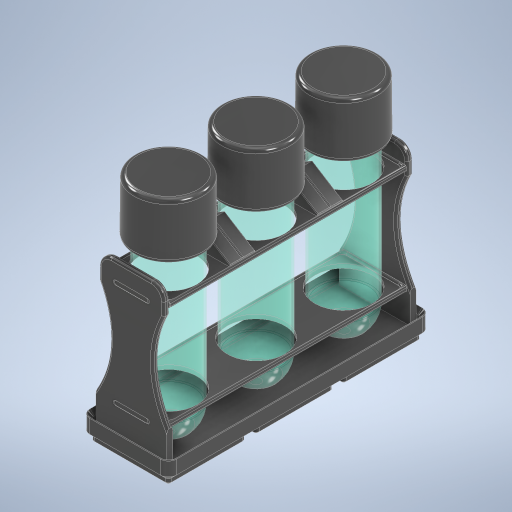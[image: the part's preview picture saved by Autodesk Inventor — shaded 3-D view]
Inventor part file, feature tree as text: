
AUTODESK INVENTOR PART (.ipt)
format: ipt  version: 2023 (Build 270158030, 158C)  size: 1,601,024 bytes
history: native  units: mm
features: extrude x23, sketch x21, other x17, fillet x17, projected_geometry x8, plane x6, chamfer x4, pattern_linear x3, mirror x2
ambient origin geometry x8: Origin, YZ Plane, XZ Plane, XY Plane, X Axis, Y Axis, Z Axis, Center Point
bodies: Body1 (feature_tree), Body2 (feature_tree), Body3 (feature_tree), Body4 (feature_tree), Body5 (feature_tree), Body6 (feature_tree), Body7 (feature_tree), Body8 (feature_tree), Body9 (feature_tree), Body10 (feature_tree), Body11 (feature_tree)
feature tree (101):
  other  "rack"
  extrude  "base-generic"  Depth=41.5mm
  extrude  "Extrusion8"  Depth=2.25mm TaperAngle=0.0deg
  extrude  "Extrusion9"  Depth=2.15mm
  extrude  "Extrusion10"  Depth=0.8mm
  extrude  "Extrusion11"  Depth=7.75mm
  extrude  "Extrusion12"  Depth=7.75mm
  plane  "Work Plane3"
  extrude  "Extrusion15"  Depth=2.4mm TaperAngle=0.0deg
  fillet  "Fillet3"  Radius=3.0mm
  extrude  "Extrusion16"  Depth=10.0mm
  fillet  "Fillet4"  Radius=2.25mm
  extrude  "Extrusion17"  Depth=35.592094mm
  fillet  "Fillet5"  Radius=15.0mm
  pattern_linear  "Rectangular Pattern1"  Spacing1=20.75mm  [1 undecoded]
  plane  "Work Plane8"
  sketch  "Sketch17"  dims[d66=7.75mm d67=2.4mm d68=0.0mm d69=3.0mm]
  extrude  "Extrusion18"  Depth=0.3mm
  pattern_linear  "Rectangular Pattern2"  Spacing1=26.75mm  [1 undecoded]
  plane  "Work Plane4"
  extrude  "Extrusion19"  Depth=2.0mm
  plane  "Work Plane6"
  extrude  "Extrusion21"  Depth=0.3mm
  extrude  "Extrusion20"  Depth=0.3mm TaperAngle=0.0deg
  fillet  "Fillet6"  Radius=9.0mm
  extrude  "Extrusion22"  Depth=0.3mm TaperAngle=0.0deg
  fillet  "Fillet7"  Radius=30.0mm
  extrude  "Extrusion28"  Depth=0.3mm
  fillet  "Fillet14"  Radius=1.0mm
  fillet  "Fillet15"  Radius=1.0mm
  pattern_linear  "Rectangular Pattern3"  Spacing1=68.75mm  [1 undecoded]
  extrude  "Extrusion23"  Depth=2.0mm
  extrude  "Extrusion24"  Depth=0.3mm
  extrude  "Extrusion25"  Depth=2.0mm TaperAngle=0.0deg
  extrude  "Extrusion26"  Depth=0.3mm
  fillet  "Fillet9"  Radius=55.0mm
  mirror  "Mirror2"
  fillet  "Fillet10"  Radius=73.0mm
  fillet  "Fillet13"  Radius=46.0mm
  extrude  "Extrusion27"  Depth=2.0mm TaperAngle=0.0deg
  chamfer  "Chamfer3"  Distance=6.0mm
  chamfer  "Chamfer4"  [1 undecoded]
  fillet  "Fillet12"  Radius=6.9mm
  fillet  "Fillet16"  Radius=6.9mm
  extrude  "Extrusion29"  Depth=0.3mm
  chamfer  "Chamfer5"  Distance=2.0mm
  chamfer  "Chamfer6"  Distance=1.0mm
  extrude  "Extrusion30"  Depth=0.3mm
  plane  "Work Plane9"
  mirror  "Mirror4"
  fillet  "Fillet19"  Radius=50.0mm
  fillet  "Fillet20"  Radius=14.0mm
  fillet  "Fillet21"  Radius=14.0mm
  fillet  "Fillet22"  Radius=3.1mm
  fillet  "Fillet18"  Radius=6.0mm
  extrude  "fill-gaps"  Depth=0.3mm
  sketch  "Sketch9"  dims[d50=41.5mm d51=41.5mm]
  sketch  "Sketch10"  dims[d52=3.75mm d53=2.25mm d54=0.0mm]
  projected_geometry  "Projected Loop2"
  sketch  "Sketch11"  dims[d55=3.75mm d56=2.15mm d57=-7.853982mm]
  projected_geometry  "Projected Loop3"
  sketch  "Sketch12"  dims[d58=1.8mm d59=0.0mm d60=0.8mm d61=-7.853982mm]
  projected_geometry  "Projected Loop4"
  sketch  "Sketch13"  dims[d62=6.5mm d63=7.75mm]
  sketch  "Sketch14"  dims[d64=7.75mm d65=7.75mm]
  sketch  "Sketch19"  dims[d70=6.0mm d71=0.0mm d72=30.0mm d74=42.0mm d75=10.0mm d77=42.0mm d79=2.25mm d80=0.0mm]
  other  "test-tube"
  sketch  "Sketch20"  dims[d82=3.75mm d84=35.592094mm d92=15.0mm]
  other  "tt-lid"
  sketch  "Sketch21"  dims[d95=12.0mm]
  other  "Pattern of test-tube:1"
  other  "TT-2"
  other  "Pattern of test-tube:2"
  other  "TT-3"
  other  "Pattern of tt-lid:3"
  other  "lid-2"
  other  "Pattern of tt-lid:4"
  other  "lid-3"
  plane  "Work Plane5"
  sketch  "Sketch23"  dims[d97=1.5mm]
  projected_geometry  "Projected Loop5"
  sketch  "Sketch25"  dims[d98=1.5mm]
  other  "tth-side"
  other  "tt-toprack"
  other  "Pattern of tt-toprack:6"
  other  "tt-rack-bottom"
  sketch  "Sketch26"  dims[d99=13.0mm]
  sketch  "Sketch28"  dims[d100=13.0mm]
  sketch  "Sketch29"  dims[d105=25.9mm]
  sketch  "Sketch30"  dims[d112=81.5mm d113=0.0mm]
  sketch  "Sketch31"  dims[d114=12.9mm]
  projected_geometry  "Projected Loop6"
  projected_geometry  "Projected Loop7"
  other  "Pattern of tth-side:7"
  other  "ttr-side-b"
  sketch  "Sketch32"  dims[d116=78.0mm]
  projected_geometry  "Projected Loop8"
  sketch  "Sketch33"  dims[d117=41.5mm]
  projected_geometry  "Projected Loop9"
  sketch  "Sketch34"  dims[d118=41.5mm]
  sketch  "Sketch35"  dims[d119=20.75mm d120=20.75mm d121=33.1mm d122=26.75mm d123=-0.087266mm d124=2.0mm d125=18.0mm d126=3.0mm d127=0.0mm d128=9.0mm d129=2.9mm d130=0.0mm d131=30.0mm d133=42.0mm d135=1.0mm d136=1.0mm d137=1.0mm d138=68.75mm d139=0.0mm d140=2.0mm d141=0.8mm d142=2.0mm d143=0.0mm d144=20.0mm d146=50.0mm d147=55.0mm d148=23.0mm d149=73.0mm d150=46.0mm d151=2.0mm d152=0.0mm d153=6.0mm d155=-3.0mm d156=6.9mm d157=6.9mm d158=2.1mm d159=2.0mm d160=0.0mm d164=1.0mm d165=2.1mm d167=50.0mm d169=14.0mm d170=14.0mm d171=3.1mm d172=6.0mm d173=3.1mm d174=6.0mm d175=0.0mm d176=0.0mm d180=3.0mm d181=0.0mm d182=4.5mm d183=0.0mm d184=1.95mm d185=0.0mm d186=3.0mm d187=12.75mm d188=12.75mm d189=6.0mm d190=0.9mm d191=1.0mm d193=2.15mm d194=4.65mm d195=0.0mm d196=1.9mm d197=2.0mm d198=45.0deg d199=0.7mm d200=2.0mm d201=45.0deg d202=0.3mm d203=0.9mm d204=1.0mm d205=1.0mm d206=1.0mm d207=1.0mm d208=1.0mm d209=0.0mm d210=2.0mm d211=0.9mm d212=0.2mm d214=15.0mm d215=15.0mm d216=15.0mm d217=15.0mm d218=10.0mm d219=0.0mm d220=14.6mm d221=9.0mm d222=30.0deg d223=14.6mm d224=9.0mm d225=30.0deg d228=5.75mm d229=5.75mm d230=0.5mm d231=5.75mm d232=5.75mm d233=0.5mm d234=0.0mm d236=0.3mm d237=0.25mm d238=0.3mm d239=0.2mm d240=0.2mm d17=0.5mm d18=0.872665mm d19=0.5mm d20=0.872665mm d24=0.0mm d25=0.0mm d26=0.0mm d27=0.0mm]
note: 4 required parameter values undecoded (feature->parameter linkage not recoverable at this tier; creation-order binding heuristic only, values carry confidence <= 0.55)
